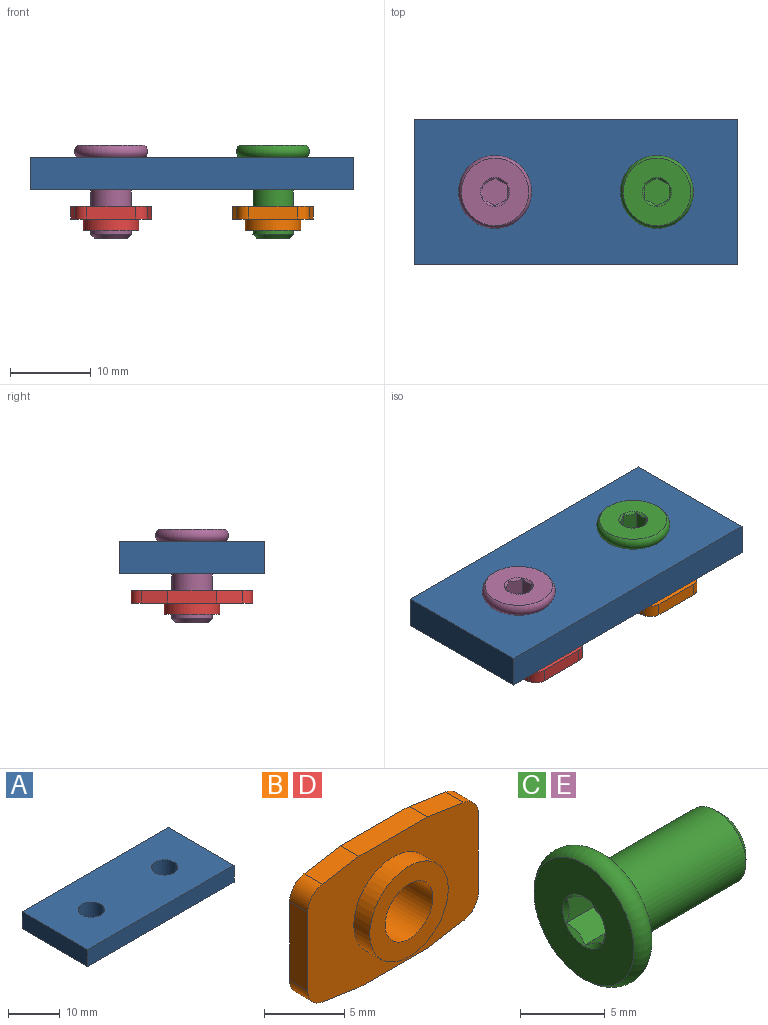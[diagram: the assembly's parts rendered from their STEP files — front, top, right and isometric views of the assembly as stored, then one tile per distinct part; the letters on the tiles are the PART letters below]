
ASSEMBLY  parts=5 mates=4
PART A: 8 faces, bbox 40x18x4 mm
  f0: cylinder r=2.55mm len=5.1mm, axis (0,0,-1), area 64.1mm2, adj f2,f3
  f1: cylinder r=2.55mm len=5.1mm, axis (0,0,-1), area 64.1mm2, adj f2,f3
  f2: plane 40x18mm, normal (0,0,1), area 679.1mm2, adj f0,f1,f4,f5,f6,f7
  f3: plane 40x18mm, normal (0,0,-1), area 679.1mm2, adj f0,f1,f4,f5,f6,f7
  f4: plane 18x4mm, normal (-1,0,0), area 72mm2, adj f2,f3,f5,f7
  f5: plane 40x4mm, normal (0,-1,0), area 160mm2, adj f2,f3,f4,f6
  f6: plane 18x4mm, normal (1,0,0), area 72mm2, adj f2,f3,f5,f7
  f7: plane 40x4mm, normal (0,1,0), area 160mm2, adj f2,f3,f4,f6
PART B: 17 faces, bbox 15x3x10 mm
  f0: cylinder r=2.1mm len=4.2mm, axis (0,-1,0), area 39.6mm2, adj f15,f16
  f1: cylinder r=3.45mm len=6.9mm, axis (0,1,0), area 30.3mm2, adj f2,f16
  f2: plane 15x10mm, normal (0,-1,0), area 104.8mm2, adj f1,f3,f4,f5,f6,f7,f8,f9
  f3: cylinder r=1.5mm len=1.6mm, axis (0,1,0), area 3.4mm2, adj f2,f4,f14,f15
  f4: plane 3.24x1.6mm, normal (0.16,0,0.99), area 5.2mm2, adj f2,f3,f5,f15
  f5: plane 6x1.6mm, normal (0,0,1), area 9.6mm2, adj f2,f4,f6,f15
  f6: plane 3.24x1.6mm, normal (-0.16,0,0.99), area 5.2mm2, adj f2,f5,f7,f15
  f7: cylinder r=1.5mm len=1.6mm, axis (0,1,0), area 3.4mm2, adj f2,f6,f8,f15
  f8: plane 6x1.6mm, normal (-1,0,0), area 9.6mm2, adj f2,f7,f9,f15
  f9: cylinder r=1.5mm len=1.6mm, axis (0,1,0), area 3.4mm2, adj f2,f8,f10,f15
  f10: plane 3.24x1.6mm, normal (-0.16,0,-0.99), area 5.2mm2, adj f2,f9,f11,f15
  f11: plane 6x1.6mm, normal (0,0,-1), area 9.6mm2, adj f2,f10,f12,f15
  f12: plane 3.24x1.6mm, normal (0.16,0,-0.99), area 5.2mm2, adj f2,f11,f13,f15
  f13: cylinder r=1.5mm len=1.6mm, axis (0,1,0), area 3.4mm2, adj f2,f12,f14,f15
  f14: plane 6x1.6mm, normal (1,0,0), area 9.6mm2, adj f2,f3,f13,f15
  f15: plane 15x10mm, normal (0,1,0), area 128.3mm2, adj f0,f3,f4,f5,f6,f7,f8,f9
  f16: plane 6.9x6.9mm, normal (0,-1,0), area 23.5mm2, adj f0,f1
PART C: 14 faces, bbox 11.8x9.7x9.7 mm
  f0: cone r=1.78mm half-angle=45deg, axis (-1,0,0), area 3.1mm2, adj f5,f8,f9,f10,f11,f12,f13
  f1: torus R=3.5mm, axis (1,0,0), area 46.7mm2, adj f5,f6
  f2: cone r=2mm half-angle=45deg, axis (-1,0,0), area 10mm2, adj f3,f4
  f3: cylinder r=2.5mm len=9.5mm, axis (1,0,0), area 149.2mm2, adj f2,f6
  f4: plane 4x4mm, normal (1,0,0), area 12.6mm2, adj f2
  f5: plane 8.32x8.32mm, normal (-1,0,0), area 44.4mm2, adj f0,f1
  f6: plane 8.32x8.32mm, normal (1,0,0), area 34.8mm2, adj f1,f3
  f7: plane 3.46x3mm, normal (-1,0,0), area 7.8mm2, adj f8,f9,f10,f11,f12,f13
  f8: plane 2.25x1.5mm, normal (0,-0.5,-0.87), area 3.6mm2, adj f0,f7,f9,f13
  f9: plane 2.25x1.73mm, normal (0,-1,0), area 3.6mm2, adj f0,f7,f8,f10
  f10: plane 2.25x1.5mm, normal (0,-0.5,0.87), area 3.6mm2, adj f0,f7,f9,f11
  f11: plane 2.25x1.5mm, normal (0,0.5,0.87), area 3.6mm2, adj f0,f7,f10,f12
  f12: plane 2.25x1.73mm, normal (0,1,0), area 3.6mm2, adj f0,f7,f11,f13
  f13: plane 2.25x1.5mm, normal (0,0.5,-0.87), area 3.6mm2, adj f0,f7,f8,f12
PART D: same geometry as B
PART E: same geometry as C
PLACE A at identity fixed
PLACE B rot(axis=(0.58,-0.58,-0.58),120deg) t=(10,0,-2)mm
PLACE C rot(axis=(0.58,0.58,-0.58),120deg) t=(10,0,-4)mm
PLACE D rot(axis=(0.58,-0.58,-0.58),120deg) t=(-10,0,-2)mm
PLACE E rot(axis=(0.58,0.58,-0.58),120deg) t=(-10,0,-4)mm
MATE fastened D.f0 <-> A.f1  axis (0,0,1) through (-10,0,-2)mm
MATE fastened E.f0 <-> A.f1  axis (0,0,-1) through (-10,0,4)mm
MATE fastened C.f0 <-> A.f0  axis (0,0,-1) through (10,0,4)mm
MATE fastened B.f0 <-> A.f0  axis (0,0,1) through (10,0,-2)mm
